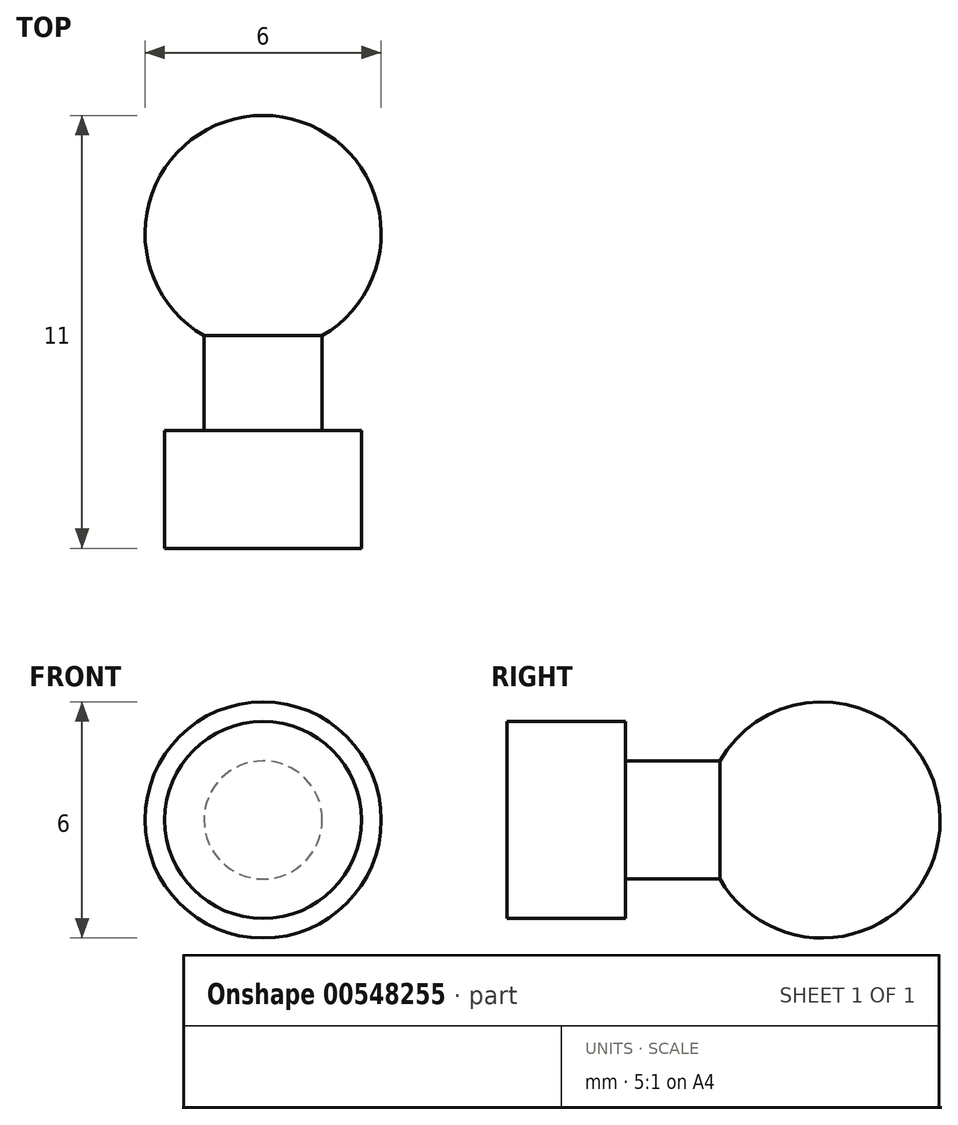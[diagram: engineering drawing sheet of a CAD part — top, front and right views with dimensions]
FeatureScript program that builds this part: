
annotation { "Feature Type Name" : "Feature", "Feature Type Description" : "" }
export const myFeature = defineFeature(function(context is Context, id is Id, definition is map)
    precondition{}
    {
        {
            var Q0;
            Q0=qCreatedBy(makeId("Right.planeOp"),FACE);
            var sketch = newSketch(context, id + "F0", { "sketchPlane" : qUnion([Q0])});
            skLineSegment(sketch, "E0", {"start": v(5.5, 0) * mm, "end": v(-5.5, 0) * mm});
            skLineSegment(sketch, "E1", {"start": v(-5.5, 0) * mm, "end": v(-5.5, 2.5) * mm});
            skLineSegment(sketch, "E2", {"start": v(-5.5, 2.5) * mm, "end": v(-2.5, 2.5) * mm});
            skLineSegment(sketch, "E3", {"start": v(-2.5, 2.5) * mm, "end": v(-2.5, 1.5) * mm});
            skLineSegment(sketch, "E4", {"start": v(-2.5, 1.5) * mm, "end": v(-0.1, 1.5) * mm});
            skArc(sketch, "E5", {"start": v(5.5, 0) * mm, "mid": v(3.28, 2.9) * mm, "end": v(-0.1, 1.5) * mm});
            skSolve(sketch);
        }
        {
            var Q0;
            Q0=makeQuery(id+"F0.imprint","IMPRINT",FACE,{"disambiguationData":[TD([[makeQuery(id+"F0.imprint","IMPRINT",EDGE,{"derivedFrom":sQuery(id+"F0.wireOp",EDGE,"E0")}),-1.0]])]});
            var Q1;
            Q1=sQuery(id+"F0.wireOp",EDGE,"E0");
            revolve(context, id + "F1", {"entities" : qUnion([Q0]), "axis" : qUnion([Q1]), "revolveType" : RevolveType.FULL});
        }
    });
